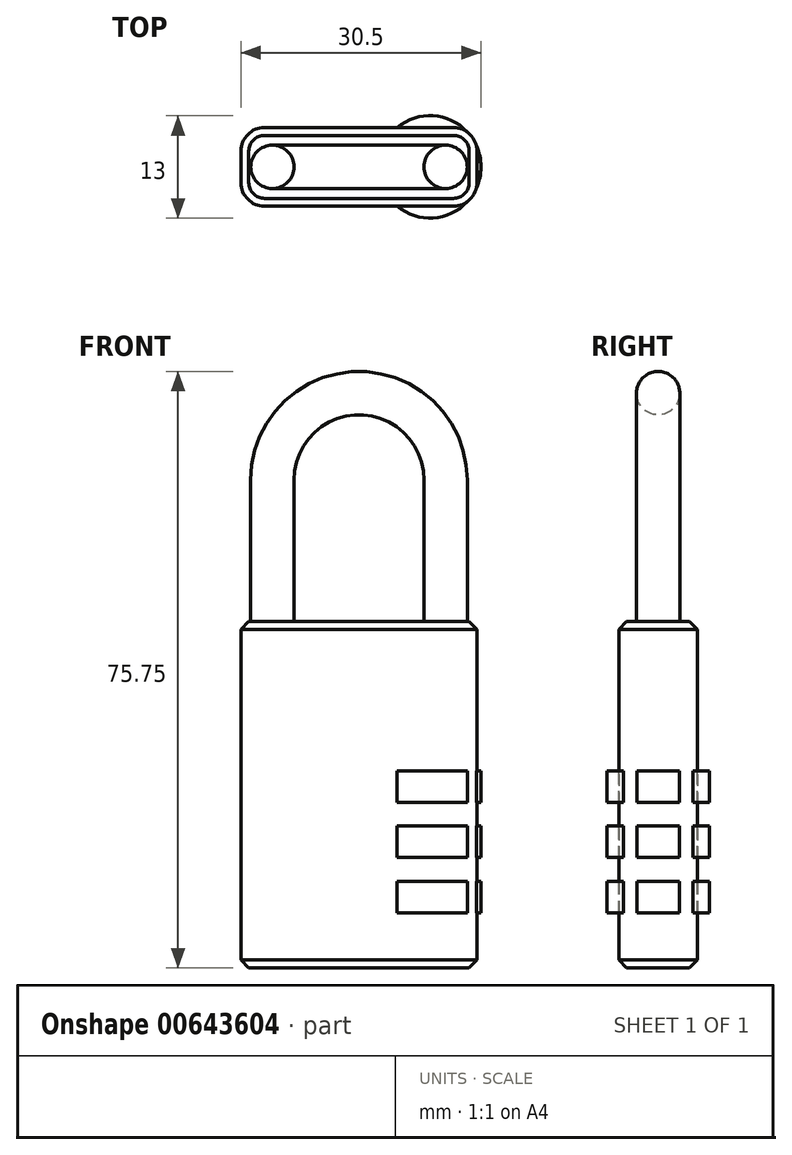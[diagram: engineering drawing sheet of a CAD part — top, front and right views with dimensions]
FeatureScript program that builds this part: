
annotation { "Feature Type Name" : "Feature", "Feature Type Description" : "" }
export const myFeature = defineFeature(function(context is Context, id is Id, definition is map)
    precondition{}
    {
        {
            var Q0;
            Q0=qCreatedBy(makeId("Top.planeOp"),FACE);
            var sketch = newSketch(context, id + "F0", { "sketchPlane" : qUnion([Q0])});
            skLineSegment(sketch, "E0.bottom", {"start": v(15, 5) * mm, "end": v(-15, 5) * mm});
            skLineSegment(sketch, "E0.top", {"start": v(15, -5) * mm, "end": v(-15, -5) * mm});
            skLineSegment(sketch, "E0.left", {"start": v(15, 5) * mm, "end": v(15, -5) * mm});
            skLineSegment(sketch, "E0.right", {"start": v(-15, 5) * mm, "end": v(-15, -5) * mm});
            skPoint(sketch, "E0.middle", {"position": v(0, 0) * mm});
            skSolve(sketch);
        }
        {
            var Q0;
            Q0=makeQuery(id+"F0.imprint","IMPRINT",FACE,{"disambiguationData":[TD([[makeQuery(id+"F0.imprint","IMPRINT",EDGE,{"derivedFrom":sQuery(id+"F0.wireOp",EDGE,"E0.bottom")}),1.0]])]});
            extrude(context, id + "F1", {"entities" : qUnion([Q0]), "depth" : 44 * mm, "offsetDistance" : 25 * mm});
        }
        {
            var Q0;
            Q0=makeQuery(id+"F1.opExtrude","SWEPT_EDGE",EDGE,{"disambiguationData":[OSD([sQuery(id+"F0.wireOp",EDGE,"E0.top"),sQuery(id+"F0.wireOp",EDGE,"E0.left")])]});
            var Q1;
            Q1=makeQuery(id+"F1.opExtrude","SWEPT_EDGE",EDGE,{"disambiguationData":[OSD([sQuery(id+"F0.wireOp",EDGE,"E0.top"),sQuery(id+"F0.wireOp",EDGE,"E0.right")])]});
            fillet(context, id + "F2", {"entities" : qUnion([Q0, Q1]), "radius" : 3 * mm, "tangentPropagation" : true, "allowEdgeOverflow" : false});
        }
        {
            var Q0;
            Q0=makeQuery(id+"F1.opExtrude","SWEPT_EDGE",EDGE,{"disambiguationData":[OSD([sQuery(id+"F0.wireOp",EDGE,"E0.bottom"),sQuery(id+"F0.wireOp",EDGE,"E0.left")])]});
            var Q1;
            Q1=makeQuery(id+"F1.opExtrude","SWEPT_EDGE",EDGE,{"disambiguationData":[OSD([sQuery(id+"F0.wireOp",EDGE,"E0.bottom"),sQuery(id+"F0.wireOp",EDGE,"E0.right")])]});
            fillet(context, id + "F3", {"entities" : qUnion([Q0, Q1]), "radius" : 3 * mm, "tangentPropagation" : true, "allowEdgeOverflow" : false});
        }
        {
            var Q0;
            Q0=qCreatedBy(makeId("Top.planeOp"),FACE);
            var sketch = newSketch(context, id + "F4", { "sketchPlane" : qUnion([Q0])});
            skCircle(sketch, "E1", {"center": v(-11, 0) * mm, "radius": 2.75 * mm});
            skCircle(sketch, "E2", {"center": v(11, 0) * mm, "radius": 2.75 * mm});
            skSolve(sketch);
        }
        {
            var Q0;
            Q0 = qSketchRegion(id + "F4", true);
            var Q1;
            Q1=sQuery(id+"F4.wireOp",EDGE,"E2");
            extrude(context, id + "F5", {"entities" : qUnion([Q0]), "operationType" : NewBodyOperationType.ADD, "surfaceEntities" : qUnion([Q1]), "depth" : 62 * mm, "offsetDistance" : 25 * mm, "hasSecondDirection" : true, "secondDirectionOppositeDirection" : false, "secondDirectionDepth" : 44 * mm});
        }
        {
            var Q0;
            Q0=qCreatedBy(makeId("Top.planeOp"),FACE);
            cPlane(context, id + "F6", {"entities" : qUnion([Q0]), "cplaneType" : CPlaneType.OFFSET, "offset" : 62 * mm, "width" : 150 * mm, "height" : 150 * mm});
        }
        {
            var Q0;
            Q0=qCreatedBy(id+"F6.planeOp",FACE);
            var sketch = newSketch(context, id + "F7", { "sketchPlane" : qUnion([Q0])});
            skCircle(sketch, "E3", {"center": v(11, 0) * mm, "radius": 2.75 * mm});
            skLineSegment(sketch, "E4", {"start": v(0, -6.13) * mm, "end": v(0, 2.96) * mm});
            skSolve(sketch);
        }
        {
            var Q0;
            Q0 = qSketchRegion(id + "F7", true);
            var Q1;
            Q1=sQuery(id+"F7.wireOp",EDGE,"E4");
            revolve(context, id + "F8", {"operationType" : NewBodyOperationType.ADD, "entities" : qUnion([Q0]), "axis" : qUnion([Q1]), "revolveType" : RevolveType.ONE_DIRECTION, "oppositeDirection" : true, "angle" : 180 * degree});
        }
        {
            var Q0;
            Q0=qCreatedBy(makeId("Right.planeOp"),FACE);
            cPlane(context, id + "F9", {"entities" : qUnion([Q0]), "cplaneType" : CPlaneType.OFFSET, "offset" : 9 * mm, "width" : 150 * mm, "height" : 150 * mm});
        }
        {
            var Q0;
            Q0=qCreatedBy(id+"F9.planeOp",FACE);
            var sketch = newSketch(context, id + "F10", { "sketchPlane" : qUnion([Q0])});
            skLineSegment(sketch, "E5.bottom", {"start": v(0, 7) * mm, "end": v(-6.5, 7) * mm});
            skLineSegment(sketch, "E5.top", {"start": v(0, 11) * mm, "end": v(-6.5, 11) * mm});
            skLineSegment(sketch, "E5.left", {"start": v(0, 7) * mm, "end": v(0, 11) * mm});
            skLineSegment(sketch, "E5.right", {"start": v(-6.5, 7) * mm, "end": v(-6.5, 11) * mm});
            skLineSegment(sketch, "E6.bottom", {"start": v(0, 14) * mm, "end": v(-6.5, 14) * mm});
            skLineSegment(sketch, "E6.top", {"start": v(0, 18) * mm, "end": v(-6.5, 18) * mm});
            skLineSegment(sketch, "E6.left", {"start": v(0, 14) * mm, "end": v(0, 18) * mm});
            skLineSegment(sketch, "E6.right", {"start": v(-6.5, 14) * mm, "end": v(-6.5, 18) * mm});
            skLineSegment(sketch, "E7.bottom", {"start": v(0, 21) * mm, "end": v(-6.5, 21) * mm});
            skLineSegment(sketch, "E7.top", {"start": v(0, 25) * mm, "end": v(-6.5, 25) * mm});
            skLineSegment(sketch, "E7.left", {"start": v(0, 21) * mm, "end": v(0, 25) * mm});
            skLineSegment(sketch, "E7.right", {"start": v(-6.5, 21) * mm, "end": v(-6.5, 25) * mm});
            skLineSegment(sketch, "E8", {"start": v(0, 25.51) * mm, "end": v(0, 0) * mm});
            skSolve(sketch);
        }
        {
            var Q0;
            Q0 = qSketchRegion(id + "F10", true);
            var Q1;
            Q1=sQuery(id+"F10.wireOp",EDGE,"E8");
            revolve(context, id + "F11", {"operationType" : NewBodyOperationType.ADD, "entities" : qUnion([Q0]), "axis" : qUnion([Q1]), "revolveType" : RevolveType.FULL});
        }
        {
            var Q0;
            Q0=makeQuery(id+"F1.opExtrude","CAP_EDGE",EDGE,{"disambiguationData":[OSD([sQuery(id+"F0.wireOp",EDGE,"E0.left")])],"isStart":false});
            var Q1;
            {var subQ0=sQuery(id+"F0.wireOp",EDGE,"E0.left");var subQ1=sQuery(id+"F0.wireOp",EDGE,"E0.bottom");Q1=makeQuery(id+"F3.opFillet","BLEND_EDGE",EDGE,{"blendedFrom":[makeQuery(id+"F1.opExtrude","SWEPT_EDGE",EDGE,{"disambiguationData":[OSD([subQ1,subQ0])]}),makeQuery(id+"F1.opExtrude","CAP_FACE",FACE,{"disambiguationData":[OSD([subQ1,sQuery(id+"F0.wireOp",EDGE,"E0.top"),subQ0,sQuery(id+"F0.wireOp",EDGE,"E0.right")])],"isStart":false})],"blendedInto":[makeQuery(id+"F1.opExtrude","CAP_FACE",FACE,{"disambiguationData":[OSD([subQ1,sQuery(id+"F0.wireOp",EDGE,"E0.top"),subQ0,sQuery(id+"F0.wireOp",EDGE,"E0.right")])],"isStart":false})]});}
            var Q2;
            {var subQ0=sQuery(id+"F0.wireOp",EDGE,"E0.left");var subQ1=sQuery(id+"F0.wireOp",EDGE,"E0.top");Q2=makeQuery(id+"F2.opFillet","BLEND_EDGE",EDGE,{"blendedFrom":[makeQuery(id+"F1.opExtrude","SWEPT_EDGE",EDGE,{"disambiguationData":[OSD([subQ1,subQ0])]}),makeQuery(id+"F1.opExtrude","CAP_FACE",FACE,{"disambiguationData":[OSD([sQuery(id+"F0.wireOp",EDGE,"E0.bottom"),subQ1,subQ0,sQuery(id+"F0.wireOp",EDGE,"E0.right")])],"isStart":false})],"blendedInto":[makeQuery(id+"F1.opExtrude","CAP_FACE",FACE,{"disambiguationData":[OSD([sQuery(id+"F0.wireOp",EDGE,"E0.bottom"),subQ1,subQ0,sQuery(id+"F0.wireOp",EDGE,"E0.right")])],"isStart":false})]});}
            var Q3;
            {var subQ0=sQuery(id+"F0.wireOp",EDGE,"E0.right");var subQ1=sQuery(id+"F0.wireOp",EDGE,"E0.bottom");Q3=makeQuery(id+"F3.opFillet","BLEND_EDGE",EDGE,{"blendedFrom":[makeQuery(id+"F1.opExtrude","SWEPT_EDGE",EDGE,{"disambiguationData":[OSD([subQ1,subQ0])]}),makeQuery(id+"F1.opExtrude","CAP_FACE",FACE,{"disambiguationData":[OSD([subQ1,sQuery(id+"F0.wireOp",EDGE,"E0.top"),sQuery(id+"F0.wireOp",EDGE,"E0.left"),subQ0])],"isStart":false})],"blendedInto":[makeQuery(id+"F1.opExtrude","CAP_FACE",FACE,{"disambiguationData":[OSD([subQ1,sQuery(id+"F0.wireOp",EDGE,"E0.top"),sQuery(id+"F0.wireOp",EDGE,"E0.left"),subQ0])],"isStart":false})]});}
            var Q4;
            Q4=makeQuery(id+"F1.opExtrude","CAP_EDGE",EDGE,{"disambiguationData":[OSD([sQuery(id+"F0.wireOp",EDGE,"E0.right")])],"isStart":false});
            var Q5;
            {var subQ0=sQuery(id+"F0.wireOp",EDGE,"E0.right");var subQ1=sQuery(id+"F0.wireOp",EDGE,"E0.top");Q5=makeQuery(id+"F2.opFillet","BLEND_EDGE",EDGE,{"blendedFrom":[makeQuery(id+"F1.opExtrude","SWEPT_EDGE",EDGE,{"disambiguationData":[OSD([subQ1,subQ0])]}),makeQuery(id+"F1.opExtrude","CAP_FACE",FACE,{"disambiguationData":[OSD([sQuery(id+"F0.wireOp",EDGE,"E0.bottom"),subQ1,sQuery(id+"F0.wireOp",EDGE,"E0.left"),subQ0])],"isStart":false})],"blendedInto":[makeQuery(id+"F1.opExtrude","CAP_FACE",FACE,{"disambiguationData":[OSD([sQuery(id+"F0.wireOp",EDGE,"E0.bottom"),subQ1,sQuery(id+"F0.wireOp",EDGE,"E0.left"),subQ0])],"isStart":false})]});}
            chamfer(context, id + "F12", {"entities" : qUnion([Q0, Q1, Q2, Q3, Q4, Q5]), "width" : 1 * mm, "tangentPropagation" : true});
        }
        {
            var Q0;
            Q0=makeQuery(id+"F1.opExtrude","CAP_FACE",FACE,{"disambiguationData":[OSD([sQuery(id+"F0.wireOp",EDGE,"E0.bottom"),sQuery(id+"F0.wireOp",EDGE,"E0.top"),sQuery(id+"F0.wireOp",EDGE,"E0.left"),sQuery(id+"F0.wireOp",EDGE,"E0.right")])],"isStart":true});
            chamfer(context, id + "F13", {"entities" : qUnion([Q0]), "width" : 1 * mm, "tangentPropagation" : true});
        }
    });
